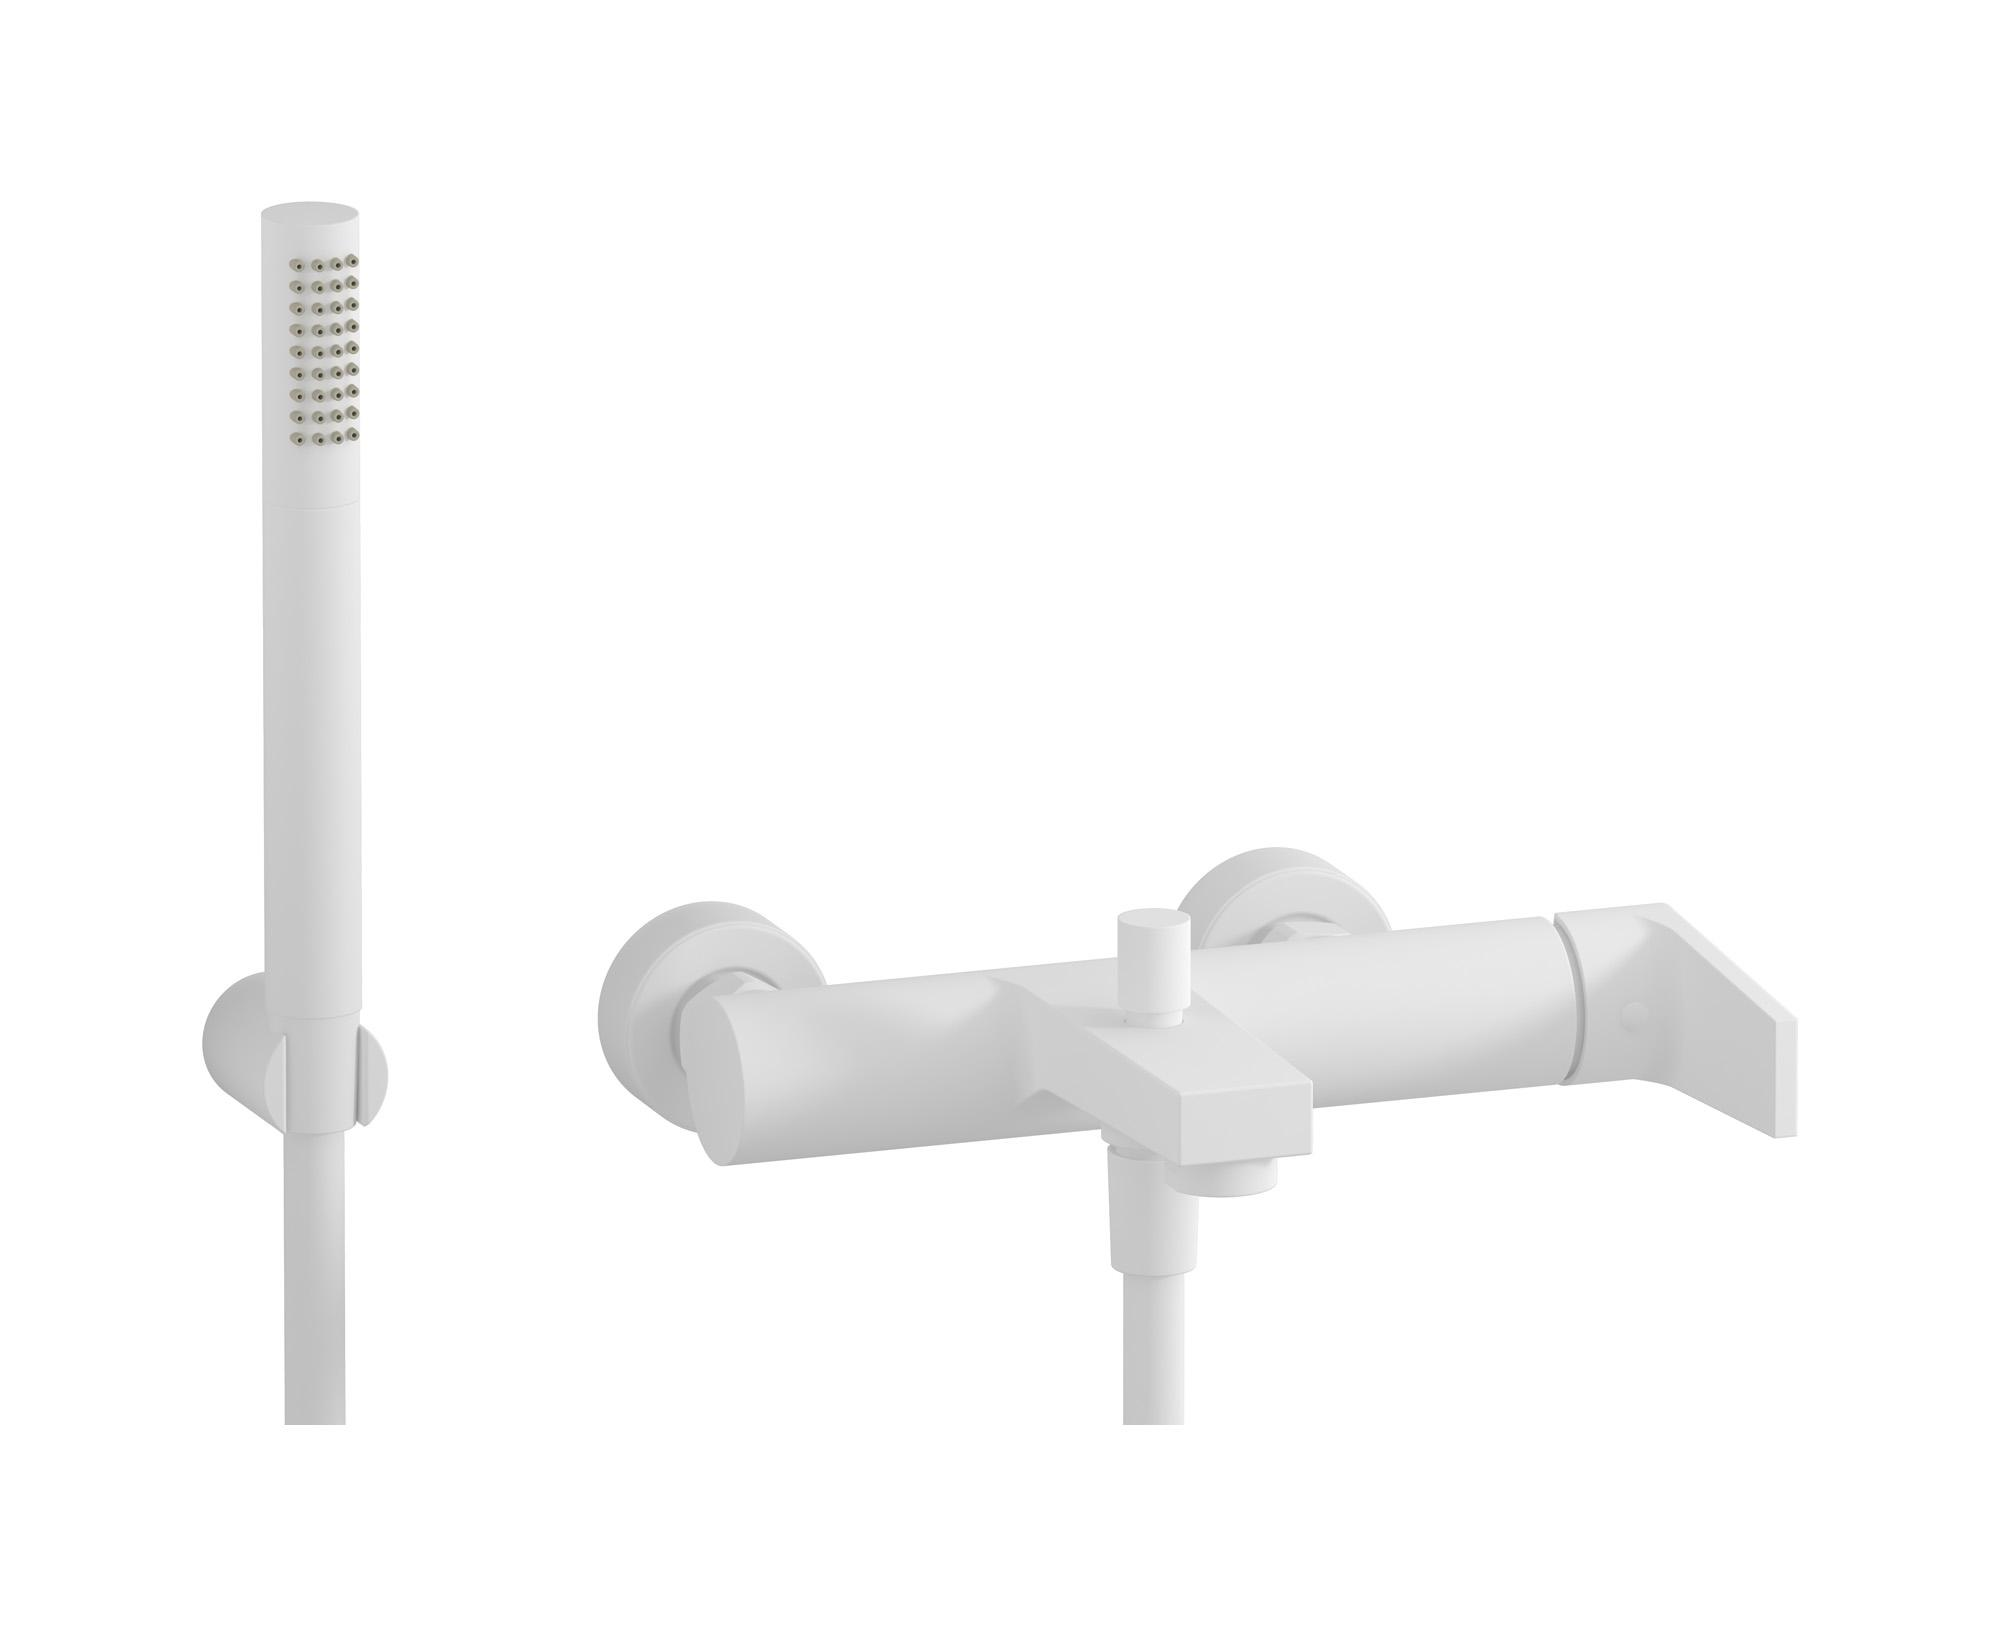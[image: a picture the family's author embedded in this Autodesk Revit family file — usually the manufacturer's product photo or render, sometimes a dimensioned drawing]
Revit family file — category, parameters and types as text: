
# Revit family: TW250
name_source: partatom
category: Apparecchi idraulici
units: mm (PartAtom-declared; Revit-internal decimal feet)

## family parameters
Basato su piano di lavoro = No
Condiviso = No
Mantieni orientamento annotazione = No
Numero OmniClass = 23.45.55.17
Punto di calcolo locali = No
Quota connettore circolare = Usa diametro
Sempre verticale = Sì
Taglio con vuoti quando caricato = No
Tipo di parte = Normale
Titolo OmniClass = Mixing Faucets

## types (12) — shared parameters
Cold water inlet = 10 mm  [stored 0.0328084 ft]
Commenti sul tipo = Bath filler
Connessione CW = No
Connessione HW = No
Connessione di scarico = No
Connessione di ventilazione = No
Descrizione = Wall mounted bath filler complete with shower kit
Hot water inlet = 10 mm  [stored 0.0328084 ft]
Produttore = IB Rubinetterie S.p.A.
URL = https://www.weareib.it
zero-valued in all types: Prospetto di default

## per-type parameters (varying)
| type | Finishes surface | Immagine tipo | Modello |
| Chrome | IB_Chrome | TW250CC.jpg | TW250CC |
| Matt black | IB_matt black | TW250NP.jpg | TW250NP |
| Matt white | IB_matt white | TW250BO.jpg | TW250BO |
| Brushed nickel | IB_Brushed nickel | TW250SS.jpg | TW250SS |
| Black chrome | IB_Black chrome | TW250CF.jpg | TW250CF |
| Brushed black chrome | IB_Brushed black chrome | TW250CS.jpg | TW250CS |
| Pale gold | IB_Pale gold | TW250II.jpg | TW250II |
| Brushed pale gold | IB_brushed pale gold | TW250IS.jpg | TW250IS |
| Rose gold | IB_Rose gold | TW250RS.jpg | TW250RS |
| Brushed rose gold | IB_Brushed rose gold | TW250SR.jpg | TW250SR |
| Gold | IB_gold | TW250OO.jpg | TW250OO |
| Brushed gold | IB_brushed gold | TW250OS.jpg | TW250OS |

note: [stored X ft] marks values corroborated as IEEE doubles in the binary element streams (Revit-internal decimal feet)
